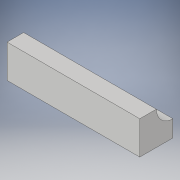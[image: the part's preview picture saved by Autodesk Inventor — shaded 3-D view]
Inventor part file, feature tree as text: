
AUTODESK INVENTOR PART (.ipt)
format: ipt  version: 2019.1 (Build 231200000, 200)  size: 95,744 bytes
history: native  units: in
note: dims shown in document units (in); Inventor stores cm internally (conversion verified against a paired STEP export)
features: extrude x1, sketch x1
ambient origin geometry x8: Origin, YZ Plane, XZ Plane, XY Plane, X Axis, Y Axis, Z Axis, Center Point
bodies: Solid1 (feature_tree)
feature tree (2):
  extrude  "Extrusion1"  Depth=1.5in
  sketch  "Sketch1"  dims[d0=1.5in d1=1.5in d2=1.5in d3=6.0in d4=0.0in d5=1.5in d6=1.5in]
